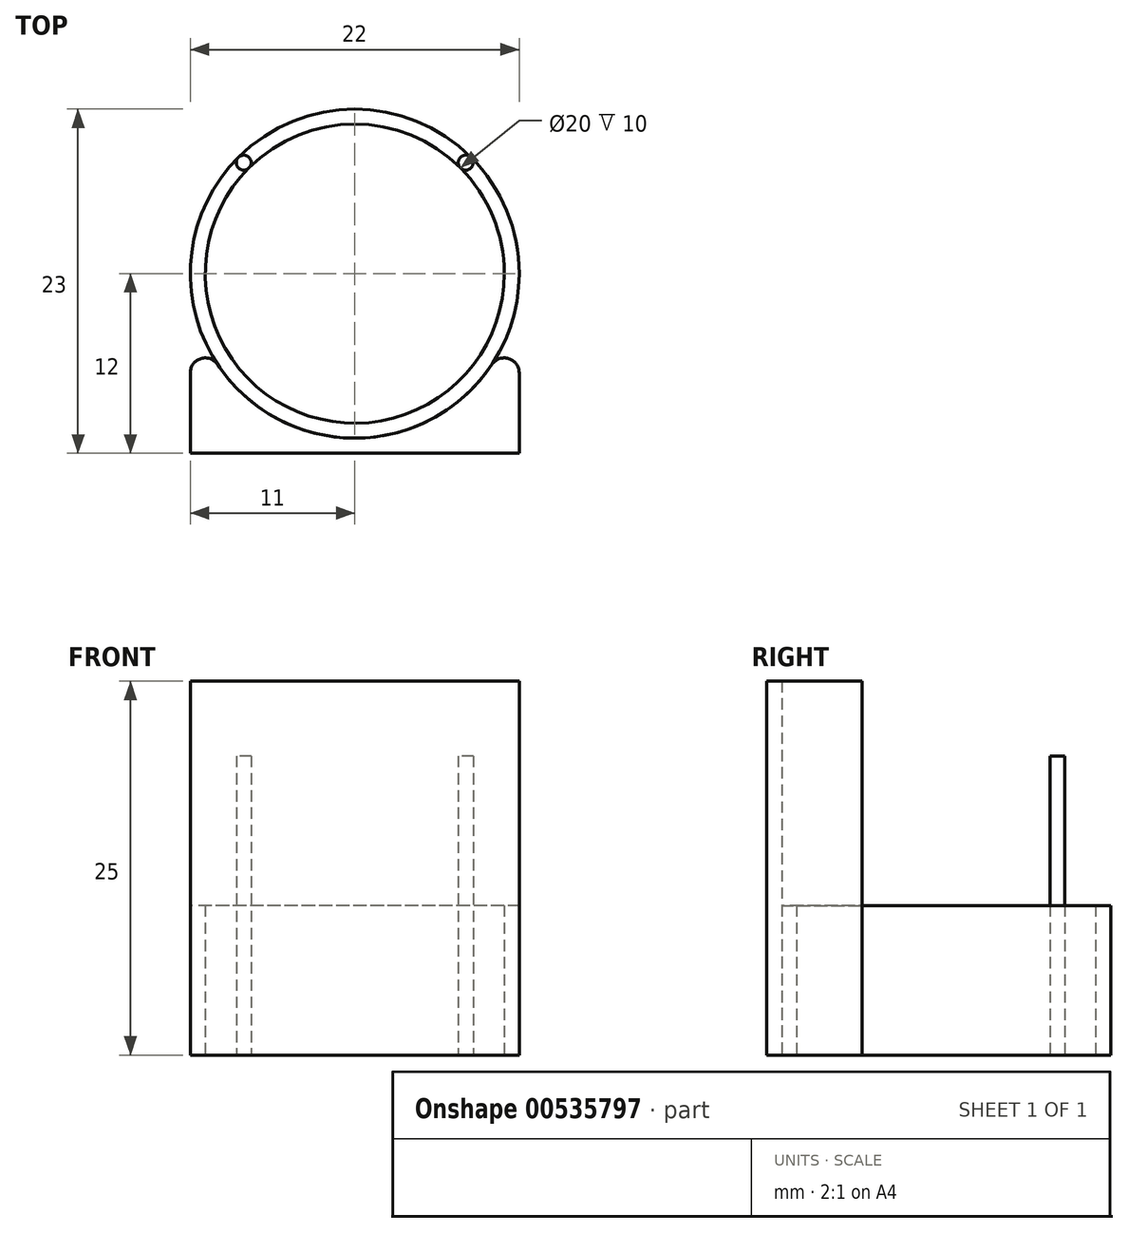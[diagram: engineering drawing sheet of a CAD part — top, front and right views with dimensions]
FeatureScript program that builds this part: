
annotation { "Feature Type Name" : "Feature", "Feature Type Description" : "" }
export const myFeature = defineFeature(function(context is Context, id is Id, definition is map)
    precondition{}
    {
        {
            var Q0;
            Q0=qCreatedBy(makeId("Top.planeOp"),FACE);
            var sketch = newSketch(context, id + "F0", { "sketchPlane" : qUnion([Q0])});
            skCircle(sketch, "E0", {"center": v(0, 0) * mm, "radius": 10 * mm});
            skCircle(sketch, "E1", {"center": v(0, 0) * mm, "radius": 11 * mm});
            skSolve(sketch);
        }
        {
            var Q0;
            Q0=qCreatedBy(makeId("Top.planeOp"),FACE);
            var sketch = newSketch(context, id + "F1", { "sketchPlane" : qUnion([Q0])});
            skLineSegment(sketch, "E2", {"start": v(0, 0) * mm, "end": v(-7.42, 7.42) * mm, "construction": true});
            skLineSegment(sketch, "E3", {"start": v(0, 0) * mm, "end": v(7.42, 7.42) * mm, "construction": true});
            skLineSegment(sketch, "E4", {"start": v(0, 0) * mm, "end": v(-17.43, 0) * mm, "construction": true});
            skCircle(sketch, "E5", {"center": v(-7.42, 7.42) * mm, "radius": 0.5 * mm});
            skCircle(sketch, "E6", {"center": v(7.42, 7.42) * mm, "radius": 0.5 * mm});
            skSolve(sketch);
        }
        {
            var Q0;
            Q0 = qSketchRegion(id + "F1", true);
            extrude(context, id + "F2", {"entities" : qUnion([Q0]), "depth" : 20 * mm, "offsetDistance" : 25 * mm});
        }
        {
            var Q0;
            Q0=makeQuery(id+"F0.imprint","IMPRINT",FACE,{"disambiguationData":[TD([[makeQuery(id+"F0.imprint","IMPRINT",EDGE,{"derivedFrom":sQuery(id+"F0.wireOp",EDGE,"E0")}),-1.0]])]});
            extrude(context, id + "F3", {"entities" : qUnion([Q0]), "depth" : 10 * mm, "offsetDistance" : 25 * mm});
        }
        {
            var Q0;
            Q0=makeQuery(id+"F0.imprint","IMPRINT",FACE,{"disambiguationData":[TD([[makeQuery(id+"F0.imprint","IMPRINT",EDGE,{"derivedFrom":sQuery(id+"F0.wireOp",EDGE,"E0")}),-1.0]])]});
            var sketch = newSketch(context, id + "F4", { "sketchPlane" : qUnion([Q0])});
            skLineSegment(sketch, "E7", {"start": v(-11, 0) * mm, "end": v(-11, -12) * mm});
            skLineSegment(sketch, "E8", {"start": v(11, 0) * mm, "end": v(11, -12) * mm});
            skLineSegment(sketch, "E9", {"start": v(-11, -12) * mm, "end": v(11, -12) * mm});
            skSolve(sketch);
        }
        {
            var Q0;
            Q0 = qSketchRegion(id + "F4", true);
            var Q1;
            {var subQ0=sQuery(id+"F4.wireOp",EDGE,"E7");Q1=makeQuery(id+"F4.imprint","IMPRINT",FACE,{"disambiguationData":[TD([[makeQuery(id+"F4.imprint","IMPRINT",EDGE,{"derivedFrom":subQ0}),1.0]])]});}
            extrude(context, id + "F5", {"entities" : qUnion([Q0, Q1]), "depth" : 25 * mm, "offsetDistance" : 25 * mm});
        }
        {
            var Q0;
            Q0=makeQuery(id+"F5.opExtrude","SWEPT_EDGE",EDGE,{"disambiguationData":[OSD([sQuery(id+"F0.wireOp",EDGE,"E1"),sQuery(id+"F4.wireOp",EDGE,"E7")])]});
            var Q1;
            Q1=makeQuery(id+"F5.opExtrude","SWEPT_EDGE",EDGE,{"disambiguationData":[OSD([sQuery(id+"F0.wireOp",EDGE,"E1"),sQuery(id+"F4.wireOp",EDGE,"E8")])]});
            fillet(context, id + "F6", {"entities" : qUnion([Q0, Q1]), "radius" : 1 * mm, "tangentPropagation" : true, "allowEdgeOverflow" : false});
        }
    });
